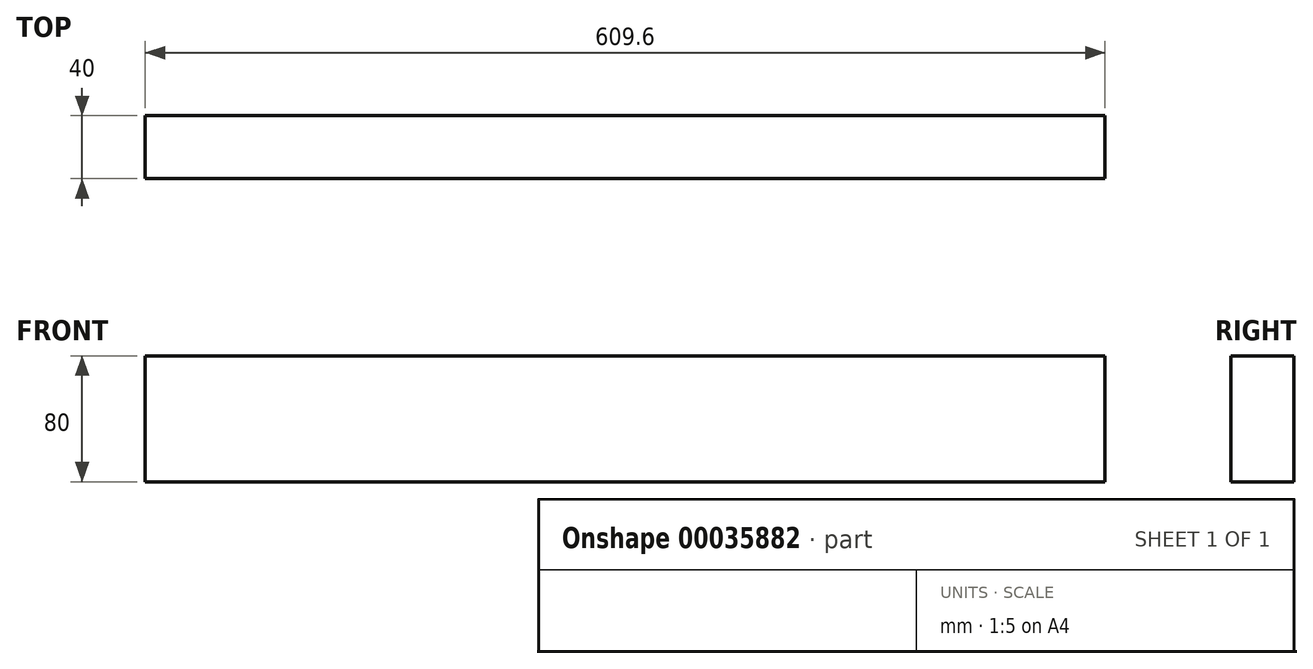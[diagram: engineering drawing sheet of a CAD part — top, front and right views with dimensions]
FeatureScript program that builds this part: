
annotation { "Feature Type Name" : "Feature", "Feature Type Description" : "" }
export const myFeature = defineFeature(function(context is Context, id is Id, definition is map)
    precondition{}
    {
        {
            var Q0;
            Q0=qCreatedBy(makeId("Right.planeOp"),FACE);
            var sketch = newSketch(context, id + "F0", { "sketchPlane" : qUnion([Q0])});
            skLineSegment(sketch, "E0.bottom", {"start": v(-928.82, -372.69) * mm, "end": v(-888.82, -372.69) * mm});
            skLineSegment(sketch, "E0.top", {"start": v(-928.82, -452.69) * mm, "end": v(-888.82, -452.69) * mm});
            skLineSegment(sketch, "E0.left", {"start": v(-928.82, -372.69) * mm, "end": v(-928.82, -452.69) * mm});
            skLineSegment(sketch, "E0.right", {"start": v(-888.82, -372.69) * mm, "end": v(-888.82, -452.69) * mm});
            skSolve(sketch);
        }
        {
            var Q0;
            Q0 = qSketchRegion(id + "F0", true);
            extrude(context, id + "F1", {"entities" : qUnion([Q0]), "depth" : 609.6 * mm});
        }
    });
